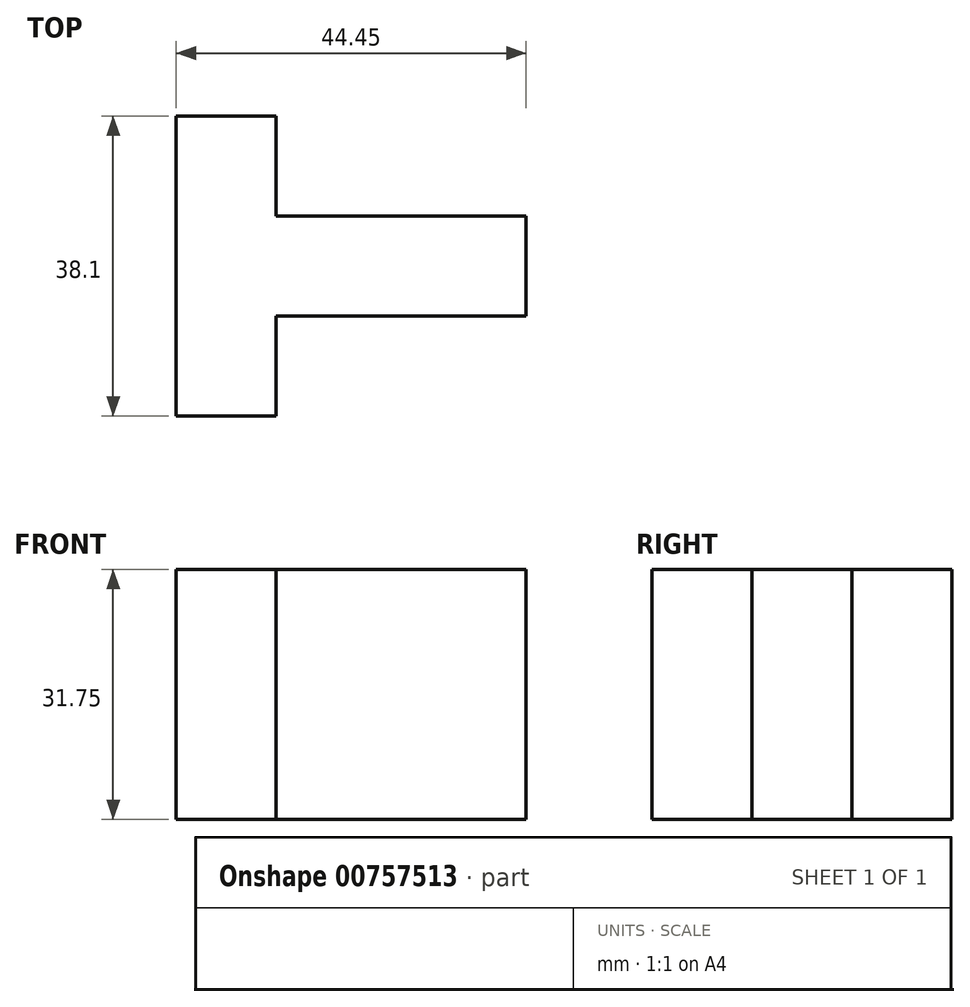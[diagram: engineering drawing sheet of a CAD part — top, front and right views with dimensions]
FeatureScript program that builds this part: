
annotation { "Feature Type Name" : "Feature", "Feature Type Description" : "" }
export const myFeature = defineFeature(function(context is Context, id is Id, definition is map)
    precondition{}
    {
        {
            var Q0;
            Q0=qCreatedBy(makeId("Front.planeOp"),FACE);
            var sketch = newSketch(context, id + "F0", { "sketchPlane" : qUnion([Q0])});
            skLineSegment(sketch, "E0", {"start": v(0, -2.4) * mm, "end": v(0, 31.75) * mm});
            skLineSegment(sketch, "E1", {"start": v(0, 31.75) * mm, "end": v(-44.45, 31.75) * mm});
            skLineSegment(sketch, "E2", {"start": v(-44.45, 31.75) * mm, "end": v(-44.45, 0) * mm});
            skLineSegment(sketch, "E3", {"start": v(-44.45, 0) * mm, "end": v(0, 0) * mm});
            skSolve(sketch);
        }
        {
            var Q0;
            Q0 = qSketchRegion(id + "F0", true);
            extrude(context, id + "F1", {"entities" : qUnion([Q0]), "depth" : 25.4 * mm, "offsetDistance" : 25.4 * mm});
        }
        {
            var Q0;
            Q0=makeQuery(id+"F1.opExtrude","CAP_FACE",FACE,{"disambiguationData":[OSD([sQuery(id+"F0.wireOp",EDGE,"E0"),sQuery(id+"F0.wireOp",EDGE,"E1"),sQuery(id+"F0.wireOp",EDGE,"E2"),sQuery(id+"F0.wireOp",EDGE,"E3")])],"isStart":false});
            var sketch = newSketch(context, id + "F2", { "sketchPlane" : qUnion([Q0])});
            skLineSegment(sketch, "E4", {"start": v(-31.75, 0) * mm, "end": v(-31.75, 31.75) * mm});
            skSolve(sketch);
        }
        {
            var Q0;
            {var subQ0=sQuery(id+"F2.wireOp",EDGE,"E4");Q0=makeQuery(id+"F2.imprint","IMPRINT",FACE,{"disambiguationData":[TD([[makeQuery(id+"F2.imprint","IMPRINT",EDGE,{"derivedFrom":subQ0}),-1.0]])]});}
            extrude(context, id + "F3", {"entities" : qUnion([Q0]), "operationType" : NewBodyOperationType.REMOVE, "oppositeDirection" : true, "depth" : 12.7 * mm, "offsetDistance" : 25.4 * mm});
        }
        {
            var Q0;
            Q0=makeQuery(id+"F1.opExtrude","CAP_FACE",FACE,{"disambiguationData":[OSD([sQuery(id+"F0.wireOp",EDGE,"E0"),sQuery(id+"F0.wireOp",EDGE,"E1"),sQuery(id+"F0.wireOp",EDGE,"E2"),sQuery(id+"F0.wireOp",EDGE,"E3")])],"isStart":true});
            var sketch = newSketch(context, id + "F4", { "sketchPlane" : qUnion([Q0])});
            skLineSegment(sketch, "E5", {"start": v(31.75, 0) * mm, "end": v(31.75, 31.75) * mm});
            skSolve(sketch);
        }
        {
            var Q0;
            {var subQ0=sQuery(id+"F4.wireOp",EDGE,"E5");Q0=makeQuery(id+"F4.imprint","IMPRINT",FACE,{"disambiguationData":[TD([[makeQuery(id+"F4.imprint","IMPRINT",EDGE,{"derivedFrom":subQ0}),-1.0]])]});}
            extrude(context, id + "F5", {"entities" : qUnion([Q0]), "operationType" : NewBodyOperationType.ADD, "depth" : 12.7 * mm, "offsetDistance" : 25.4 * mm});
        }
    });
